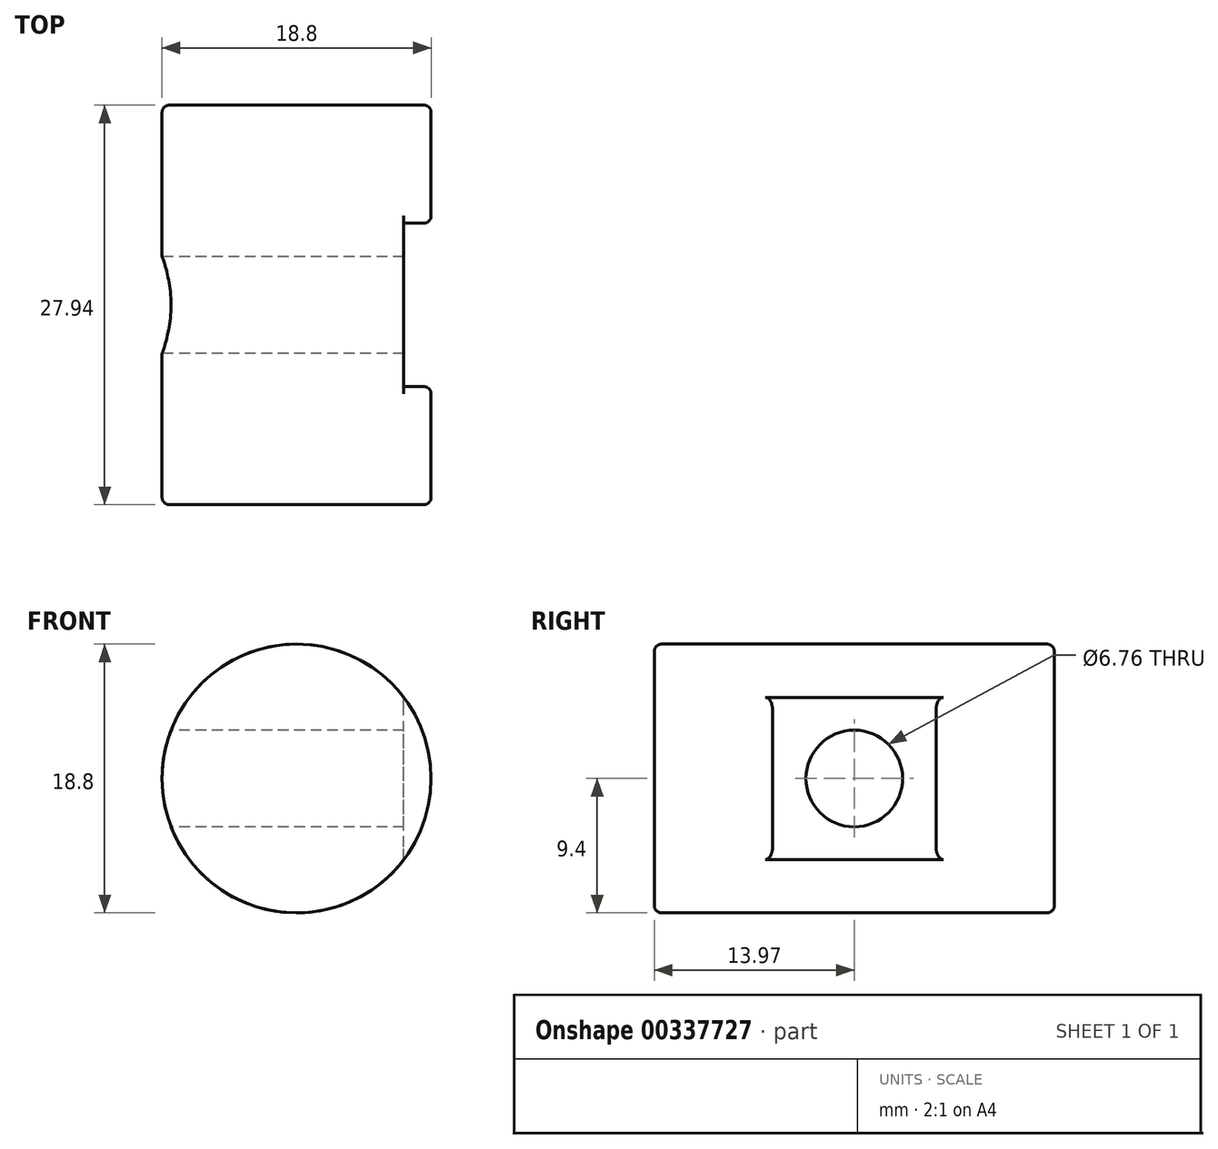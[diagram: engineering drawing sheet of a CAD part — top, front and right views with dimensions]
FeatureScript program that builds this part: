
annotation { "Feature Type Name" : "Feature", "Feature Type Description" : "" }
export const myFeature = defineFeature(function(context is Context, id is Id, definition is map)
    precondition{}
    {
        {
            var Q0;
            Q0=qCreatedBy(makeId("Front.planeOp"),FACE);
            var sketch = newSketch(context, id + "F0", { "sketchPlane" : qUnion([Q0])});
            skCircle(sketch, "E0", {"center": v(0, 0) * mm, "radius": 9.4 * mm});
            skSolve(sketch);
        }
        {
            var Q0;
            Q0=makeQuery(id+"F0.imprint","IMPRINT",FACE,{"disambiguationData":[TD([[makeQuery(id+"F0.imprint","IMPRINT",EDGE,{"derivedFrom":sQuery(id+"F0.wireOp",EDGE,"E0")}),1.0]])]});
            extrude(context, id + "F1", {"entities" : qUnion([Q0]), "depth" : 13.97 * mm, "hasSecondDirection" : true, "secondDirectionOppositeDirection" : true, "secondDirectionDepth" : 13.97 * mm});
        }
        {
            var Q0;
            Q0=qCreatedBy(makeId("Right.planeOp"),FACE);
            cPlane(context, id + "F2", {"entities" : qUnion([Q0]), "cplaneType" : CPlaneType.OFFSET, "offset" : 10.03 * mm, "width" : 152.4 * mm, "height" : 152.4 * mm});
        }
        {
            var Q0;
            Q0=qCreatedBy(id+"F2.planeOp",FACE);
            var sketch = newSketch(context, id + "F3", { "sketchPlane" : qUnion([Q0])});
            skPoint(sketch, "E1", {"position": v(0, 0) * mm});
            skSolve(sketch);
        }
        {
            var Q0;
            Q0=sQuery(id+"F3.wireOp",VERTEX,"E1");
            var Q1;
            Q1=makeQuery(id+"F1.opExtrude","SWEPT_BODY",BODY,{"disambiguationData":[OSD([sQuery(id+"F0.wireOp",EDGE,"E0")])]});
            hole(context, id + "F4", {"style" : HoleStyle.SIMPLE, "endStyle" : HoleEndStyle.THROUGH, "standardTappedOrClearance" : lookupTablePath({ "standard" : "ANSI", "fit" : "Normal (ASME)", "size" : "1/4", "type" : "Clearance" }), "standardBlindInLast" : lookupTablePath({ "fit" : "Free", "standard" : "ANSI", "size" : "1/4", "type" : "Clearance" }), "holeDiameter" : 6.76 * mm, "tappedDepth" : 20.32 * mm, "tapClearance" : 3, "locations" : qUnion([Q0]), "scope" : qUnion([Q1]), "startStyle" : HoleStartStyle.PART});
        }
        {
            var Q0;
            Q0=qCreatedBy(id+"F2.planeOp",FACE);
            var sketch = newSketch(context, id + "F5", { "sketchPlane" : qUnion([Q0])});
            skLineSegment(sketch, "E2.bottom", {"start": v(5.71, -12.67) * mm, "end": v(-5.72, -12.67) * mm});
            skLineSegment(sketch, "E2.top", {"start": v(5.72, 12.67) * mm, "end": v(-5.71, 12.67) * mm});
            skLineSegment(sketch, "E2.left", {"start": v(5.71, -12.67) * mm, "end": v(5.72, 12.67) * mm});
            skLineSegment(sketch, "E2.right", {"start": v(-5.72, -12.67) * mm, "end": v(-5.71, 12.67) * mm});
            skPoint(sketch, "E2.middle", {"position": v(0, 0) * mm});
            skSolve(sketch);
        }
        {
            var Q0;
            Q0=makeQuery(id+"F5.imprint","IMPRINT",FACE,{"disambiguationData":[TD([[makeQuery(id+"F5.imprint","IMPRINT",EDGE,{"derivedFrom":sQuery(id+"F5.wireOp",EDGE,"E2.bottom")}),-1.0]])]});
            extrude(context, id + "F6", {"entities" : qUnion([Q0]), "operationType" : NewBodyOperationType.REMOVE, "oppositeDirection" : true, "depth" : 2.54 * mm});
        }
        {
            var Q0;
            Q0=makeQuery(id+"F1.opExtrude","CAP_EDGE",EDGE,{"disambiguationData":[OSD([sQuery(id+"F0.wireOp",EDGE,"E0")])],"isStart":true});
            var Q1;
            Q1=makeQuery(id+"F1.opExtrude","CAP_EDGE",EDGE,{"disambiguationData":[OSD([sQuery(id+"F0.wireOp",EDGE,"E0")])],"isStart":false});
            var Q2;
            Q2=makeQuery(id+"F6.boolean.opBoolean","INTERSECT",EDGE,{"derivedFrom":[makeQuery(id+"F1.opExtrude","SWEPT_FACE",FACE,{"disambiguationData":[OSD([sQuery(id+"F0.wireOp",EDGE,"E0")])]}),makeQuery(id+"F6.opExtrude","SWEPT_FACE",FACE,{"disambiguationData":[OSD([sQuery(id+"F5.wireOp",EDGE,"E2.left")])]})]});
            var Q3;
            Q3=makeQuery(id+"F6.boolean.opBoolean","INTERSECT",EDGE,{"derivedFrom":[makeQuery(id+"F1.opExtrude","SWEPT_FACE",FACE,{"disambiguationData":[OSD([sQuery(id+"F0.wireOp",EDGE,"E0")])]}),makeQuery(id+"F6.opExtrude","SWEPT_FACE",FACE,{"disambiguationData":[OSD([sQuery(id+"F5.wireOp",EDGE,"E2.right")])]})]});
            fillet(context, id + "F7", {"entities" : qUnion([Q0, Q1, Q2, Q3]), "radius" : 0.5 * mm, "tangentPropagation" : true, "allowEdgeOverflow" : false});
        }
    });
